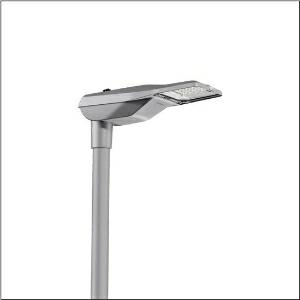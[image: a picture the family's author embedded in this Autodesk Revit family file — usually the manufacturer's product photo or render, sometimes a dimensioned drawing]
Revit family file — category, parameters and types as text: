
# Revit family: streetlight_sl_21_iq_micro___p0_8ab_5xe1r31v08db_6cb1
name_source: partatom
category: Lighting Fixtures
units: mm (PartAtom-declared; Revit-internal decimal feet)

## family parameters
Cut with Voids When Loaded = No
Host = Face
Light Source = No
Part Type = Normal
Room Calculation Point = No
Round Connector Dimension = Use Diameter
Shared = No

## types (1)
- --- (1 x LED, 4550 lm, 39.1 W, 3000K)
    Apparent Load = 39 VA
    CIE Flux Codes = 36 71 98 100 100
    Color Rendering = 70
    Color Temperature = 3000K
    Default Elevation = 1800 mm
    Description = Streetlight SL 21 iQ micro, mast luminaire, primary light control with lens, of PMMA, primary optical cover: cover, of toughened safety glass, transparent, light distribution: P0.8aB, light emission: direct distribution, primary light characteristic: asymmetric, installation type: post-top, side-entry, LED, High Power LED, rated luminous flux: 4.550lm, luminous efficacy: 116lm/W, light colour: 730, colour temperature: 3000K, control gear: iQ-Street Remote, D4i with power reduction, control: pre-setting: logarithmic dimming characteristic, Street-Remote, Auto-Match, Temp-Guard, Lumen-Switch, Night-Set, Smart-Wire, Light-Fading, Desk-Remote (wireless, voltage-free reading and setting of iQ features in the workshop via application-optimized NFC function/RFID function), optimised constant luminous flux control (CLO 2.0), mains connection: 220..240V, AC, 50/60Hz, start of lifetime: 39W, end of service life: 41W, reduction: 17W, luminaire housing, of diecast aluminium, powder-coated, Siteco® metallic grey (DB 702S), corrosivity category C5 mid according to DIN EN ISO 12944, please order mast flange separately, inclination adjustable: 0°, 5°, 10°, 15°, sealing non-destructively replaceable, multi-level sealing system, length: 528mm, width: 235mm, height: 110mm, mast flange for spigot size: 42mm (side-entry): 5XC10008XM4, 60/48mm (side-entry/post-top): 5XC10108XM2, 76/60mm (side-entry/post-top): 5XC10108XM1, mounting height: 4..8m, Smart Interface above, protection rating (complete): IP66, insulation class (complete): insulation class II (safety insulation), certification: CE, ENEC, ENEC+, VDE, impact resistance: IK10, permissible operating ambient temperature for outdoor applications: -40..+50°C, standard-compliant lighting for roads and squares, packaging unit: 1 piece

Light Distribution: P0.8aB
    Height = 110 mm
    Lamp = 1 x LED
    Lamp Light Flux = 4550 lm
    Lamp Power = 39.1 W
    Lamp count = 1
    Length = 528 mm
    Luminous efficacy = 116 lm/W
    Manufacturer = Siteco
    ModVariant = No
    Model = 5XE1R31V08DB
    Number of Poles = 1
    OnlyDefault = Yes
    Power Factor = 1
    Product Name = Streetlight SL 21 iQ micro | P0.8aB
    Product group = mast luminaire | pylon top
    ProductGroupID = 6100
    Protection Class = Protection class II
    Protection Degree = IP 66
    RLX_Detail_Level = 1
    RLX_Emergency_Light_Flux = 0 lm
    RLX_Emergency_Type = 0
    RLX_Emergency_Type_DB = No
    RlxData = <blob elided: 97921 chars, md5=39541a72>
    Socket = socket
    Standby Power = 0 W
    System Light Flux = 4550 lm
    System Power = 39 W
    Type Comments = factory setting: luminous flux: 100 % | dim-lin: 254 | 765 mA
    Type Image = l_1277292.jpg
    URL = http://relux.com
    VarID = @adj_075620
    Voltage = 0 V
    Weight = 0.00 kg
    Width = 235 mm

## geometry (parser evidence)
native form markers: Blend x4, Sweep x11
no freeform markers — native parametric forms only
